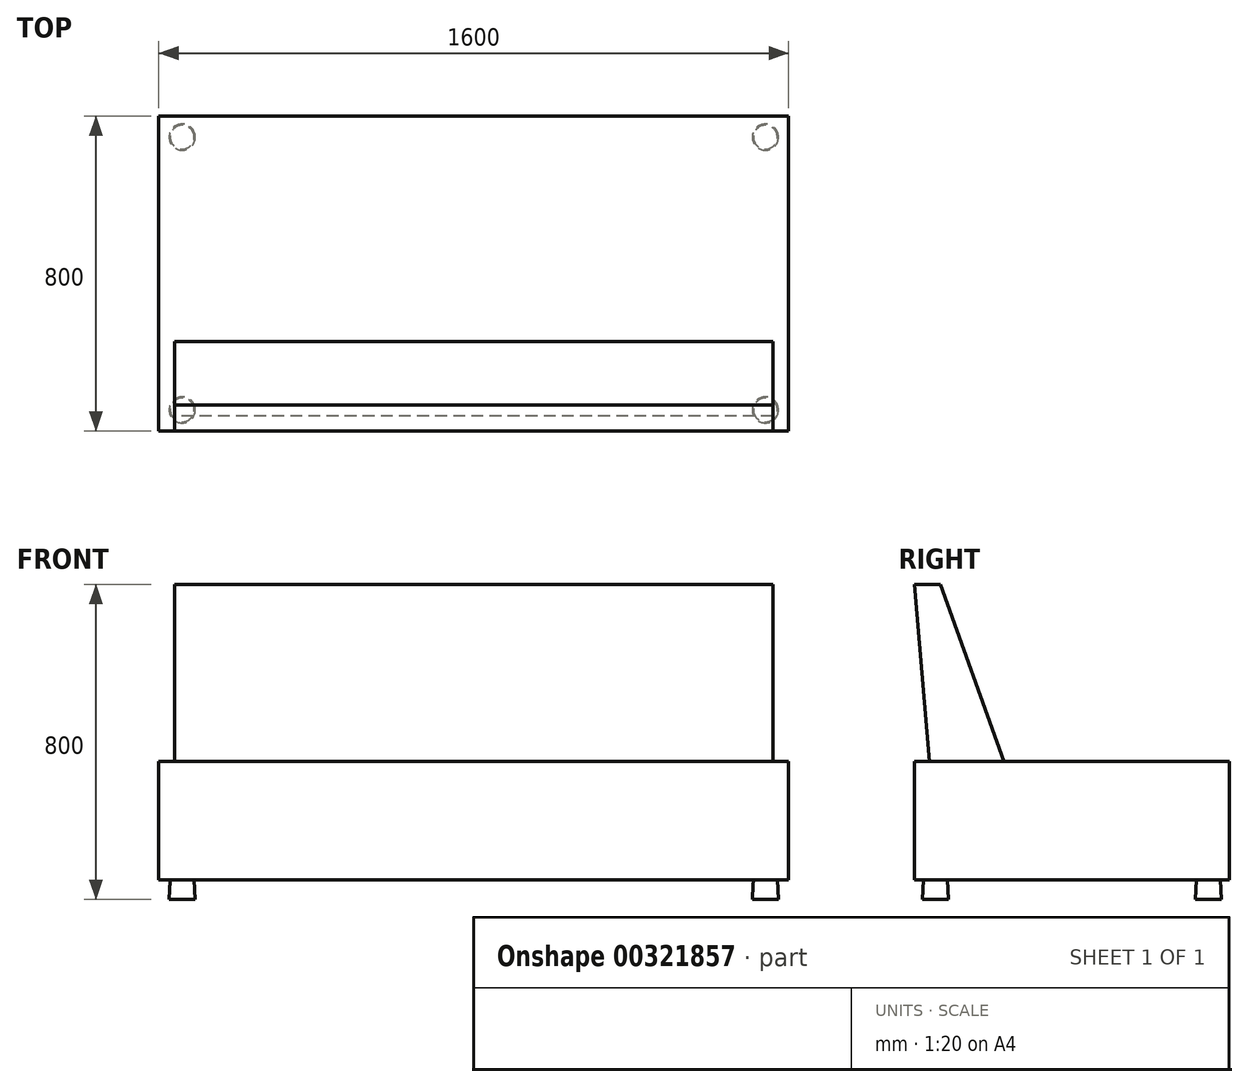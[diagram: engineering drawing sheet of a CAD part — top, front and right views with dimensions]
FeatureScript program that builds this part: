
annotation { "Feature Type Name" : "Feature", "Feature Type Description" : "" }
export const myFeature = defineFeature(function(context is Context, id is Id, definition is map)
    precondition{}
    {
        {
            var Q0;
            Q0=qCreatedBy(makeId("Top.planeOp"),FACE);
            var sketch = newSketch(context, id + "F0", { "sketchPlane" : qUnion([Q0])});
            skLineSegment(sketch, "E0.bottom", {"start": v(800, -400) * mm, "end": v(-800, -400) * mm});
            skLineSegment(sketch, "E0.top", {"start": v(800, 400) * mm, "end": v(-800, 400) * mm});
            skLineSegment(sketch, "E0.left", {"start": v(800, -400) * mm, "end": v(800, 400) * mm});
            skLineSegment(sketch, "E0.right", {"start": v(-800, -400) * mm, "end": v(-800, 400) * mm});
            skPoint(sketch, "E0.middle", {"position": v(0, 0) * mm});
            skSolve(sketch);
        }
        {
            var Q0;
            Q0=makeQuery(id+"F0.imprint","IMPRINT",FACE,{"disambiguationData":[TD([[makeQuery(id+"F0.imprint","IMPRINT",EDGE,{"derivedFrom":sQuery(id+"F0.wireOp",EDGE,"E0.bottom")}),-1.0]])]});
            extrude(context, id + "F1", {"entities" : qUnion([Q0]), "depth" : 300 * mm});
        }
        {
            var Q0;
            Q0=makeQuery(id+"F1.opExtrude","CAP_FACE",FACE,{"disambiguationData":[OSD([sQuery(id+"F0.wireOp",EDGE,"E0.bottom"),sQuery(id+"F0.wireOp",EDGE,"E0.top"),sQuery(id+"F0.wireOp",EDGE,"E0.left"),sQuery(id+"F0.wireOp",EDGE,"E0.right")])],"isStart":true});
            var sketch = newSketch(context, id + "F2", { "sketchPlane" : qUnion([Q0])});
            skLineSegment(sketch, "E1", {"start": v(-800, 0) * mm, "end": v(800, 0) * mm, "construction": true});
            skLineSegment(sketch, "E2", {"start": v(0, -400) * mm, "end": v(0, 400) * mm, "construction": true});
            skCircle(sketch, "E3", {"center": v(-740.85, -346.62) * mm, "radius": 30.5 * mm});
            skCircle(sketch, "E4.MirrorC", {"center": v(740.85, -346.62) * mm, "radius": 30.5 * mm});
            skCircle(sketch, "E5.MirrorC", {"center": v(740.85, 346.62) * mm, "radius": 30.5 * mm});
            skCircle(sketch, "E6.MirrorC", {"center": v(-740.85, 346.62) * mm, "radius": 30.5 * mm});
            skSolve(sketch);
        }
        {
            var Q0;
            Q0=qSketchRegion(id+"F2",true);
            extrude(context, id + "F3", {"entities" : qUnion([Q0]), "operationType" : NewBodyOperationType.ADD, "depth" : 50 * mm, "hasDraft" : true, "draftAngle" : 3 * degree});
        }
        {
            var Q0;
            Q0=qCreatedBy(makeId("Right.planeOp"),FACE);
            var sketch = newSketch(context, id + "F4", { "sketchPlane" : qUnion([Q0])});
            skLineSegment(sketch, "E7", {"start": v(-157, 254.91) * mm, "end": v(-334.25, 750) * mm});
            skLineSegment(sketch, "E8", {"start": v(-334.25, 750) * mm, "end": v(-400, 750) * mm});
            skLineSegment(sketch, "E9", {"start": v(-400, 750) * mm, "end": v(-355.83, 230.6) * mm});
            skLineSegment(sketch, "E10", {"start": v(-355.83, 230.6) * mm, "end": v(-157, 254.91) * mm});
            skSolve(sketch);
        }
        {
            var Q0;
            Q0=qSketchRegion(id+"F4",true);
            extrude(context, id + "F5", {"entities" : qUnion([Q0]), "operationType" : NewBodyOperationType.ADD, "endBound" : BoundingType.SYMMETRIC, "depth" : 1520 * mm});
        }
    });
